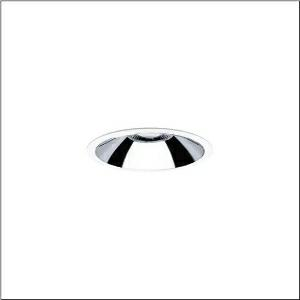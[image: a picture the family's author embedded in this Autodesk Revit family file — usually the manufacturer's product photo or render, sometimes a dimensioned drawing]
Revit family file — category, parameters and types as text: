
# Revit family: lunis_21_l_51db15dd32
name_source: partatom
category: Lighting Fixtures
units: mm (PartAtom-declared; Revit-internal decimal feet)

## family parameters
Cut with Voids When Loaded = No
Host = Face
Light Source = No
Part Type = Normal
Room Calculation Point = No
Round Connector Dimension = Use Diameter
Shared = No

## types (1)
- Lunis 21 L (1 x LED, 1670 lm, 13.8 W, 3000K)
    Apparent Load = 14 VA
    CIE Flux Codes = 90 99 100 100 100
    Color Rendering = 80
    Color Temperature = 3000K
    Default Elevation = 1800 mm
    Description = Lunis 21,  L, downlight, of PC, light emission: direct distribution, LED rated luminous flux: 1.670lm, light colour: 830, control gear: ECG DALI, with terminal, 5-pole, mains connection: 220..240V, AC, housing, round, of diecast aluminium, traffic white (RAL 9016), diameter: 162mm, protection rating (complete): IP20, insulation class (complete): insulation class II (safety insulation), certification: CE, impact resistance: IK02, packaging unit: 1 piece
    Height = 0 mm  [stored 0 ft]
    Lamp = 1 x LED
    Lamp Light Flux = 1670 lm
    Lamp Power = 13.8 W
    Lamp count = 1
    Length = 162 mm
    Luminous efficacy = 121 lm/W
    Manufacturer = Siteco
    ModVariant = No
    Model = 51DB15DD32
    Mounting Place = Ceiling
    Mounting Type = Recessed
    Number of Poles = 1
    OnlyDefault = Yes
    Power Factor = 1
    Product Name = Lunis 21 L
    Product group = downlight | ceiling recessed
    ProductGroupID = 402
    Protection Class = Protection class II
    Protection Degree = IP 20
    RLX_Detail_Level = 1
    RlxData = <blob elided: 21229 chars, md5=b925c403>
    Socket = socket
    Standby Power = 0 W
    System Light Flux = 1670 lm
    System Power = 14 W
    Type Comments = Product without accessories
    Type Image = l_1006992.jpg
    URL = http://relux.com
    VarID = ---
    Voltage = 0 V
    Weight = 0.00 kg
    Width = 0 mm  [stored 0 ft]

note: [stored X ft] marks values corroborated as IEEE doubles in the binary element streams (Revit-internal decimal feet)

## geometry (parser evidence)
native form markers: Blend x4, Sweep x13
no freeform markers — native parametric forms only
